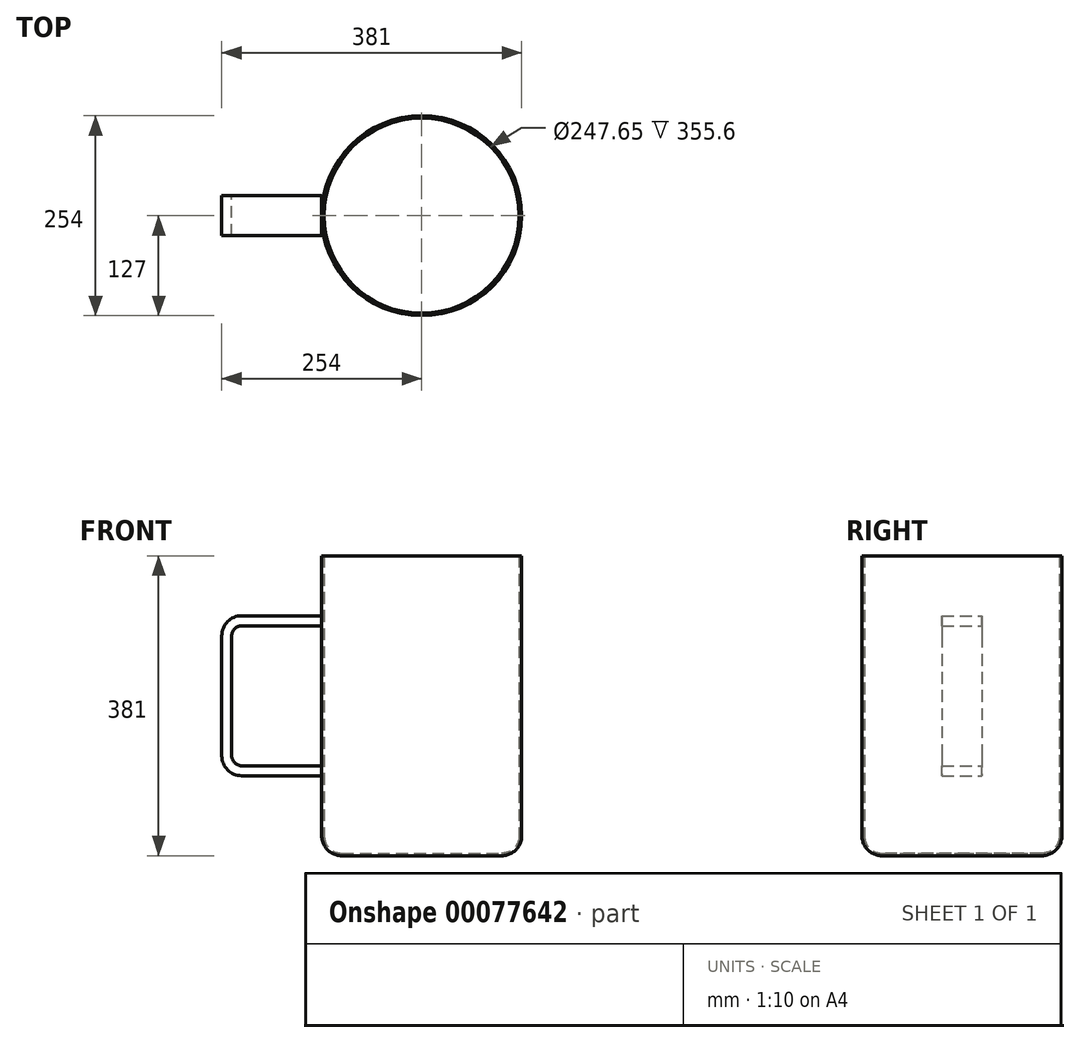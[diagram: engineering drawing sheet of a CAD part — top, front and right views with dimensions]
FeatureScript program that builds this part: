
annotation { "Feature Type Name" : "Feature", "Feature Type Description" : "" }
export const myFeature = defineFeature(function(context is Context, id is Id, definition is map)
    precondition{}
    {
        {
            var Q0;
            Q0=qCreatedBy(makeId("Front.planeOp"),FACE);
            var sketch = newSketch(context, id + "F0", { "sketchPlane" : qUnion([Q0])});
            skLineSegment(sketch, "E0", {"start": v(0, 0) * mm, "end": v(-101.6, 0) * mm});
            skLineSegment(sketch, "E1", {"start": v(-127, 25.4) * mm, "end": v(-127, 381) * mm});
            skPoint(sketch, "E2.visualSharp", {"position": v(-127, 0) * mm});
            skArc(sketch, "E2.filletArc", {"start": v(-127, 25.4) * mm, "mid": v(-119.56, 7.44) * mm, "end": v(-101.6, 0) * mm});
            skLineSegment(sketch, "E3", {"start": v(0, 0) * mm, "end": v(0, 134.02) * mm, "construction": true});
            skLineSegment(sketch, "E4.0", {"start": v(-123.83, 25.4) * mm, "end": v(-123.83, 381) * mm});
            skArc(sketch, "E4.1", {"start": v(-123.83, 25.4) * mm, "mid": v(-117.32, 9.68) * mm, "end": v(-101.6, 3.17) * mm});
            skLineSegment(sketch, "E4.2", {"start": v(0, 3.18) * mm, "end": v(-101.6, 3.17) * mm});
            skLineSegment(sketch, "E5", {"start": v(-123.83, 381) * mm, "end": v(-127, 381) * mm});
            skLineSegment(sketch, "E6", {"start": v(0, 3.18) * mm, "end": v(0, 0) * mm});
            skSolve(sketch);
        }
        {
            var Q0;
            Q0 = qSketchRegion(id + "F0", true);
            var Q1;
            Q1=sQuery(id+"F0.wireOp",EDGE,"E3");
            revolve(context, id + "F1", {"entities" : qUnion([Q0]), "axis" : qUnion([Q1]), "revolveType" : RevolveType.FULL});
        }
        {
            var Q0;
            Q0=qCreatedBy(makeId("Front.planeOp"),FACE);
            var sketch = newSketch(context, id + "F2", { "sketchPlane" : qUnion([Q0])});
            skLineSegment(sketch, "E7", {"start": v(0, 0) * mm, "end": v(-101.6, 0) * mm});
            skLineSegment(sketch, "E8", {"start": v(-127, 25.4) * mm, "end": v(-127, 381) * mm});
            skPoint(sketch, "E9.visualSharp", {"position": v(-127, 0) * mm});
            skArc(sketch, "E9.filletArc", {"start": v(-127, 25.4) * mm, "mid": v(-119.56, 7.44) * mm, "end": v(-101.6, 0) * mm});
            skLineSegment(sketch, "E10", {"start": v(0, 0) * mm, "end": v(0, 281.19) * mm, "construction": true});
            skSolve(sketch);
        }
        {
            var Q0;
            Q0=qCreatedBy(makeId("Front.planeOp"),FACE);
            var sketch = newSketch(context, id + "F3", { "sketchPlane" : qUnion([Q0])});
            skLineSegment(sketch, "E11.bottom", {"start": v(-127, 292.1) * mm, "end": v(-228.6, 292.1) * mm});
            skLineSegment(sketch, "E11.top", {"start": v(-127, 114.3) * mm, "end": v(-228.6, 114.3) * mm});
            skLineSegment(sketch, "E11.right", {"start": v(-241.3, 279.4) * mm, "end": v(-241.3, 127) * mm});
            skPoint(sketch, "E12.visualSharp", {"position": v(-241.3, 292.1) * mm});
            skArc(sketch, "E12.filletArc", {"start": v(-228.6, 292.1) * mm, "mid": v(-237.58, 288.38) * mm, "end": v(-241.3, 279.4) * mm});
            skPoint(sketch, "E13.visualSharp", {"position": v(-241.3, 114.3) * mm});
            skArc(sketch, "E13.filletArc", {"start": v(-241.3, 127) * mm, "mid": v(-237.58, 118.02) * mm, "end": v(-228.6, 114.3) * mm});
            skLineSegment(sketch, "E14.0", {"start": v(-127, 101.6) * mm, "end": v(-228.6, 101.6) * mm});
            skLineSegment(sketch, "E14.1", {"start": v(-127, 304.8) * mm, "end": v(-228.6, 304.8) * mm});
            skArc(sketch, "E14.2", {"start": v(-228.6, 304.8) * mm, "mid": v(-246.56, 297.36) * mm, "end": v(-254, 279.4) * mm});
            skLineSegment(sketch, "E14.3", {"start": v(-254, 279.4) * mm, "end": v(-254, 127) * mm});
            skArc(sketch, "E14.4", {"start": v(-254, 127) * mm, "mid": v(-246.56, 109.04) * mm, "end": v(-228.6, 101.6) * mm});
            skLineSegment(sketch, "E15", {"start": v(-127, 292.1) * mm, "end": v(-127, 304.8) * mm});
            skLineSegment(sketch, "E16", {"start": v(-127, 101.6) * mm, "end": v(-127, 114.3) * mm});
            skSolve(sketch);
        }
        {
            var Q0;
            Q0 = qSketchRegion(id + "F3", true);
            extrude(context, id + "F4", {"entities" : qUnion([Q0]), "operationType" : NewBodyOperationType.ADD, "endBound" : BoundingType.SYMMETRIC, "depth" : 50.8 * mm});
        }
    });
